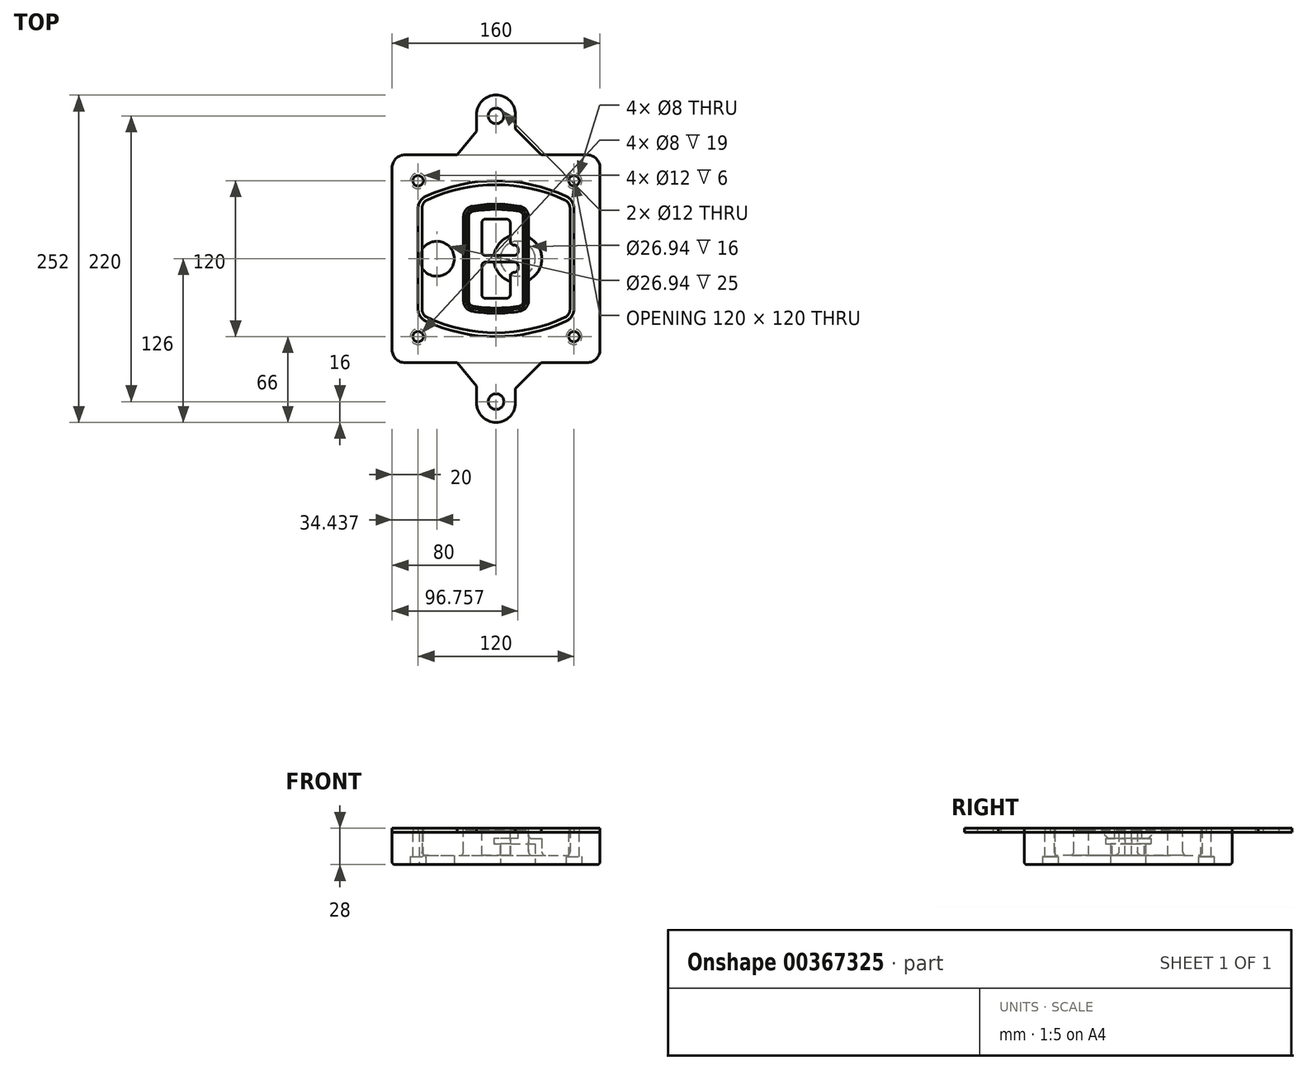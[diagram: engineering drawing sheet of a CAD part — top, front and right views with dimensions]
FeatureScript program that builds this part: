
annotation { "Feature Type Name" : "Feature", "Feature Type Description" : "" }
export const myFeature = defineFeature(function(context is Context, id is Id, definition is map)
    precondition{}
    {
        {
            var Q0;
            Q0=qCreatedBy(makeId("Top.planeOp"),FACE);
            var sketch = newSketch(context, id + "F0", { "sketchPlane" : qUnion([Q0])});
            skPoint(sketch, "E0.rect.middle", {"position": v(0, 0) * mm});
            skLineSegment(sketch, "E1.bottom", {"start": v(-70, -80) * mm, "end": v(70, -80) * mm});
            skLineSegment(sketch, "E1.top", {"start": v(-70, 80) * mm, "end": v(70, 80) * mm});
            skLineSegment(sketch, "E1.left", {"start": v(-80, -70) * mm, "end": v(-80, 70) * mm});
            skLineSegment(sketch, "E1.right", {"start": v(80, -70) * mm, "end": v(80, 70) * mm});
            skLineSegment(sketch, "E2", {"start": v(-80, 80) * mm, "end": v(80, -80) * mm, "construction": true});
            skLineSegment(sketch, "E3", {"start": v(80, 80) * mm, "end": v(-80, -80) * mm, "construction": true});
            skCircle(sketch, "E4", {"center": v(-60, 60) * mm, "radius": 4 * mm});
            skCircle(sketch, "E5", {"center": v(60, 60) * mm, "radius": 4 * mm});
            skCircle(sketch, "E6", {"center": v(60, -60) * mm, "radius": 4 * mm});
            skCircle(sketch, "E7", {"center": v(-60, -60) * mm, "radius": 4 * mm});
            skLineSegment(sketch, "E8", {"start": v(-60, 60) * mm, "end": v(60, 60) * mm, "construction": true});
            skLineSegment(sketch, "E9", {"start": v(60, 60) * mm, "end": v(60, -60) * mm, "construction": true});
            skLineSegment(sketch, "E10", {"start": v(60, -60) * mm, "end": v(-60, -60) * mm, "construction": true});
            skLineSegment(sketch, "E11", {"start": v(-60, -60) * mm, "end": v(-60, 60) * mm, "construction": true});
            skLineSegment(sketch, "E12", {"start": v(-60, 38.83) * mm, "end": v(-60, -38.83) * mm});
            skLineSegment(sketch, "E13", {"start": v(60, 38.83) * mm, "end": v(60, -38.83) * mm});
            skArc(sketch, "E14", {"start": v(54.26, 47.88) * mm, "mid": v(0, 60) * mm, "end": v(-54.26, 47.88) * mm});
            skArc(sketch, "E15", {"start": v(-54.26, -47.88) * mm, "mid": v(0, -60) * mm, "end": v(54.26, -47.88) * mm});
            skLineSegment(sketch, "E16", {"start": v(-60, 0) * mm, "end": v(60, 0) * mm, "construction": true});
            skPoint(sketch, "E17.visualSharp", {"position": v(-60, -45) * mm});
            skArc(sketch, "E17.filletArc", {"start": v(-60, -38.83) * mm, "mid": v(-58.44, -44.2) * mm, "end": v(-54.26, -47.88) * mm});
            skPoint(sketch, "E18.visualSharp", {"position": v(-60, 45) * mm});
            skArc(sketch, "E18.filletArc", {"start": v(-54.26, 47.88) * mm, "mid": v(-58.44, 44.2) * mm, "end": v(-60, 38.83) * mm});
            skPoint(sketch, "E19.visualSharp", {"position": v(60, 45) * mm});
            skArc(sketch, "E19.filletArc", {"start": v(60, 38.83) * mm, "mid": v(58.44, 44.2) * mm, "end": v(54.26, 47.88) * mm});
            skPoint(sketch, "E20.visualSharp", {"position": v(60, -45) * mm});
            skArc(sketch, "E20.filletArc", {"start": v(54.26, -47.88) * mm, "mid": v(58.44, -44.2) * mm, "end": v(60, -38.83) * mm});
            skPoint(sketch, "E21.visualSharp", {"position": v(-80, 80) * mm});
            skArc(sketch, "E21.filletArc", {"start": v(-70, 80) * mm, "mid": v(-77.07, 77.07) * mm, "end": v(-80, 70) * mm});
            skPoint(sketch, "E22.visualSharp", {"position": v(80, 80) * mm});
            skArc(sketch, "E22.filletArc", {"start": v(80, 70) * mm, "mid": v(77.07, 77.07) * mm, "end": v(70, 80) * mm});
            skPoint(sketch, "E23.visualSharp", {"position": v(80, -80) * mm});
            skArc(sketch, "E23.filletArc", {"start": v(70, -80) * mm, "mid": v(77.07, -77.07) * mm, "end": v(80, -70) * mm});
            skPoint(sketch, "E24.visualSharp", {"position": v(-80, -80) * mm});
            skArc(sketch, "E24.filletArc", {"start": v(-80, -70) * mm, "mid": v(-77.07, -77.07) * mm, "end": v(-70, -80) * mm});
            skArc(sketch, "E25.0", {"start": v(57, 38.83) * mm, "mid": v(55.9, 42.58) * mm, "end": v(52.98, 45.17) * mm});
            skLineSegment(sketch, "E25.1", {"start": v(57, 38.83) * mm, "end": v(57, -38.83) * mm});
            skArc(sketch, "E25.2", {"start": v(52.98, -45.17) * mm, "mid": v(55.9, -42.58) * mm, "end": v(57, -38.83) * mm});
            skArc(sketch, "E25.3", {"start": v(-52.98, -45.17) * mm, "mid": v(0, -57) * mm, "end": v(52.98, -45.17) * mm});
            skArc(sketch, "E25.4", {"start": v(-57, -38.83) * mm, "mid": v(-55.9, -42.58) * mm, "end": v(-52.98, -45.17) * mm});
            skArc(sketch, "E25.5", {"start": v(52.98, 45.17) * mm, "mid": v(0, 57) * mm, "end": v(-52.98, 45.17) * mm});
            skLineSegment(sketch, "E25.6", {"start": v(-57, 38.83) * mm, "end": v(-57, -38.83) * mm});
            skArc(sketch, "E25.7", {"start": v(-52.98, 45.17) * mm, "mid": v(-55.9, 42.58) * mm, "end": v(-57, 38.83) * mm});
            skArc(sketch, "E26.0", {"start": v(-55.96, 51.5) * mm, "mid": v(-61.82, 46.33) * mm, "end": v(-64, 38.83) * mm});
            skArc(sketch, "E26.1", {"start": v(55.96, 51.5) * mm, "mid": v(0, 64) * mm, "end": v(-55.96, 51.5) * mm});
            skArc(sketch, "E26.2", {"start": v(64, 38.83) * mm, "mid": v(61.82, 46.33) * mm, "end": v(55.96, 51.5) * mm});
            skLineSegment(sketch, "E26.3", {"start": v(64, 38.83) * mm, "end": v(64, -38.83) * mm});
            skArc(sketch, "E26.4", {"start": v(55.96, -51.5) * mm, "mid": v(61.82, -46.33) * mm, "end": v(64, -38.83) * mm});
            skLineSegment(sketch, "E26.5", {"start": v(-64, 38.83) * mm, "end": v(-64, -38.83) * mm});
            skArc(sketch, "E26.6", {"start": v(-55.96, -51.5) * mm, "mid": v(0, -64) * mm, "end": v(55.96, -51.5) * mm});
            skArc(sketch, "E26.7", {"start": v(-64, -38.83) * mm, "mid": v(-61.82, -46.33) * mm, "end": v(-55.96, -51.5) * mm});
            skSolve(sketch);
        }
        {
            var Q0;
            Q0=makeQuery(id+"F0.imprint","IMPRINT",FACE,{"disambiguationData":[TD([[makeQuery(id+"F0.imprint","IMPRINT",EDGE,{"derivedFrom":sQuery(id+"F0.wireOp",EDGE,"E1.bottom")}),1.0]])]});
            var Q1;
            Q1=makeQuery(id+"F0.imprint","IMPRINT",FACE,{"disambiguationData":[TD([[makeQuery(id+"F0.imprint","IMPRINT",EDGE,{"derivedFrom":sQuery(id+"F0.wireOp",EDGE,"E12")}),1.0]])]});
            var Q2;
            Q2=makeQuery(id+"F0.imprint","IMPRINT",FACE,{"disambiguationData":[TD([[makeQuery(id+"F0.imprint","IMPRINT",EDGE,{"derivedFrom":sQuery(id+"F0.wireOp",EDGE,"E25.0")}),1.0]])]});
            var Q3;
            Q3=makeQuery(id+"F0.imprint","IMPRINT",FACE,{"disambiguationData":[TD([[makeQuery(id+"F0.imprint","IMPRINT",EDGE,{"derivedFrom":sQuery(id+"F0.wireOp",EDGE,"E12")}),-1.0]])]});
            extrude(context, id + "F1", {"entities" : qUnion([Q0, Q1, Q2, Q3]), "oppositeDirection" : true, "depth" : 25 * mm});
        }
        {
            var Q0;
            Q0=makeQuery(id+"F0.imprint","IMPRINT",FACE,{"disambiguationData":[TD([[makeQuery(id+"F0.imprint","IMPRINT",EDGE,{"derivedFrom":sQuery(id+"F0.wireOp",EDGE,"E12")}),1.0]])]});
            extrude(context, id + "F2", {"entities" : qUnion([Q0]), "operationType" : NewBodyOperationType.ADD, "depth" : 3 * mm});
        }
        {
            var Q0;
            Q0=makeQuery(id+"F0.imprint","IMPRINT",FACE,{"disambiguationData":[TD([[makeQuery(id+"F0.imprint","IMPRINT",EDGE,{"derivedFrom":sQuery(id+"F0.wireOp",EDGE,"E25.0")}),1.0]])]});
            extrude(context, id + "F3", {"entities" : qUnion([Q0]), "operationType" : NewBodyOperationType.REMOVE, "oppositeDirection" : true, "depth" : 18 * mm});
        }
        {
            var Q0;
            Q0=makeQuery(id+"F2.opExtrude","CAP_FACE",FACE,{"disambiguationData":[OSD([sQuery(id+"F0.wireOp",EDGE,"E12"),sQuery(id+"F0.wireOp",EDGE,"E13"),sQuery(id+"F0.wireOp",EDGE,"E14"),sQuery(id+"F0.wireOp",EDGE,"E15"),sQuery(id+"F0.wireOp",EDGE,"E17.filletArc"),sQuery(id+"F0.wireOp",EDGE,"E18.filletArc"),sQuery(id+"F0.wireOp",EDGE,"E19.filletArc"),sQuery(id+"F0.wireOp",EDGE,"E20.filletArc"),sQuery(id+"F0.wireOp",EDGE,"E25.0"),sQuery(id+"F0.wireOp",EDGE,"E25.1"),sQuery(id+"F0.wireOp",EDGE,"E25.2"),sQuery(id+"F0.wireOp",EDGE,"E25.3"),sQuery(id+"F0.wireOp",EDGE,"E25.4"),sQuery(id+"F0.wireOp",EDGE,"E25.5"),sQuery(id+"F0.wireOp",EDGE,"E25.6"),sQuery(id+"F0.wireOp",EDGE,"E25.7")])],"isStart":false});
            var sketch = newSketch(context, id + "F4", { "sketchPlane" : qUnion([Q0])});
            skArc(sketch, "E27.0", {"start": v(-18.34, -40.45) * mm, "mid": v(0, -42) * mm, "end": v(18.34, -40.45) * mm});
            skArc(sketch, "E28.0", {"start": v(18.34, 40.45) * mm, "mid": v(0, 42) * mm, "end": v(-18.34, 40.45) * mm});
            skLineSegment(sketch, "E29", {"start": v(-25, 32.57) * mm, "end": v(-25, -32.57) * mm});
            skLineSegment(sketch, "E30", {"start": v(25, 32.57) * mm, "end": v(25, -32.57) * mm});
            skLineSegment(sketch, "E31", {"start": v(-25, 39.1) * mm, "end": v(25, 39.1) * mm, "construction": true});
            skLineSegment(sketch, "E32", {"start": v(-25, -39.1) * mm, "end": v(25, -39.1) * mm, "construction": true});
            skPoint(sketch, "E33.visualSharp", {"position": v(-25, 39.1) * mm});
            skArc(sketch, "E33.filletArc", {"start": v(-18.34, 40.45) * mm, "mid": v(-23.11, 37.73) * mm, "end": v(-25, 32.57) * mm});
            skPoint(sketch, "E34.visualSharp", {"position": v(25, 39.1) * mm});
            skArc(sketch, "E34.filletArc", {"start": v(25, 32.57) * mm, "mid": v(23.11, 37.73) * mm, "end": v(18.34, 40.45) * mm});
            skPoint(sketch, "E35.visualSharp", {"position": v(25, -39.1) * mm});
            skArc(sketch, "E35.filletArc", {"start": v(18.34, -40.45) * mm, "mid": v(23.11, -37.73) * mm, "end": v(25, -32.57) * mm});
            skPoint(sketch, "E36.visualSharp", {"position": v(-25, -39.1) * mm});
            skArc(sketch, "E36.filletArc", {"start": v(-25, -32.57) * mm, "mid": v(-23.11, -37.73) * mm, "end": v(-18.34, -40.45) * mm});
            skArc(sketch, "E37.0", {"start": v(52.98, 45.17) * mm, "mid": v(0, 57) * mm, "end": v(-52.98, 45.17) * mm});
            skArc(sketch, "E37.1", {"start": v(-52.98, 45.17) * mm, "mid": v(-55.9, 42.58) * mm, "end": v(-57, 38.83) * mm});
            skLineSegment(sketch, "E37.2", {"start": v(-57, 38.83) * mm, "end": v(-57, -38.83) * mm});
            skArc(sketch, "E37.3", {"start": v(-57, -38.83) * mm, "mid": v(-55.9, -42.58) * mm, "end": v(-52.98, -45.17) * mm});
            skArc(sketch, "E37.4", {"start": v(-52.98, -45.17) * mm, "mid": v(0, -57) * mm, "end": v(52.98, -45.17) * mm});
            skArc(sketch, "E37.5", {"start": v(52.98, -45.17) * mm, "mid": v(55.9, -42.58) * mm, "end": v(57, -38.83) * mm});
            skLineSegment(sketch, "E37.6", {"start": v(57, 38.83) * mm, "end": v(57, -38.83) * mm});
            skArc(sketch, "E37.7", {"start": v(57, 38.83) * mm, "mid": v(55.9, 42.58) * mm, "end": v(52.98, 45.17) * mm});
            skLineSegment(sketch, "E38.0", {"start": v(23, 32.57) * mm, "end": v(23, -32.57) * mm});
            skArc(sketch, "E38.1", {"start": v(18, -38.48) * mm, "mid": v(21.58, -36.44) * mm, "end": v(23, -32.57) * mm});
            skArc(sketch, "E38.2", {"start": v(-18, -38.48) * mm, "mid": v(0, -40) * mm, "end": v(18, -38.48) * mm});
            skArc(sketch, "E38.3", {"start": v(-23, -32.57) * mm, "mid": v(-21.58, -36.44) * mm, "end": v(-18, -38.48) * mm});
            skLineSegment(sketch, "E38.4", {"start": v(-23, 32.57) * mm, "end": v(-23, -32.57) * mm});
            skArc(sketch, "E38.5", {"start": v(23, 32.57) * mm, "mid": v(21.58, 36.44) * mm, "end": v(18, 38.48) * mm});
            skArc(sketch, "E38.6", {"start": v(-18, 38.48) * mm, "mid": v(-21.58, 36.44) * mm, "end": v(-23, 32.57) * mm});
            skArc(sketch, "E38.7", {"start": v(18, 38.48) * mm, "mid": v(0, 40) * mm, "end": v(-18, 38.48) * mm});
            skArc(sketch, "E39.0", {"start": v(21, 32.57) * mm, "mid": v(20.06, 35.15) * mm, "end": v(17.67, 36.5) * mm});
            skLineSegment(sketch, "E39.1", {"start": v(21, 32.57) * mm, "end": v(21, -32.57) * mm});
            skArc(sketch, "E39.2", {"start": v(17.67, -36.5) * mm, "mid": v(20.06, -35.15) * mm, "end": v(21, -32.57) * mm});
            skArc(sketch, "E39.3", {"start": v(-17.67, -36.5) * mm, "mid": v(0, -38) * mm, "end": v(17.67, -36.5) * mm});
            skArc(sketch, "E39.4", {"start": v(-21, -32.57) * mm, "mid": v(-20.06, -35.15) * mm, "end": v(-17.67, -36.5) * mm});
            skArc(sketch, "E39.5", {"start": v(17.67, 36.5) * mm, "mid": v(0, 38) * mm, "end": v(-17.67, 36.5) * mm});
            skLineSegment(sketch, "E39.6", {"start": v(-21, 32.57) * mm, "end": v(-21, -32.57) * mm});
            skArc(sketch, "E39.7", {"start": v(-17.67, 36.5) * mm, "mid": v(-20.06, 35.15) * mm, "end": v(-21, 32.57) * mm});
            skLineSegment(sketch, "E40", {"start": v(-25, 0) * mm, "end": v(25, 0) * mm, "construction": true});
            skLineSegment(sketch, "E41", {"start": v(-11, 5.5) * mm, "end": v(-11, 27.5) * mm});
            skLineSegment(sketch, "E42", {"start": v(-8, 30.5) * mm, "end": v(8, 30.5) * mm});
            skLineSegment(sketch, "E43", {"start": v(11, 27.5) * mm, "end": v(11, 13.5) * mm});
            skLineSegment(sketch, "E44", {"start": v(14, 10.5) * mm, "end": v(14, 10.5) * mm});
            skLineSegment(sketch, "E45", {"start": v(17, 7.5) * mm, "end": v(17, 5.5) * mm});
            skLineSegment(sketch, "E46", {"start": v(14, 2.5) * mm, "end": v(-8, 2.5) * mm});
            skPoint(sketch, "E47.visualSharp", {"position": v(-11, 30.5) * mm});
            skArc(sketch, "E47.filletArc", {"start": v(-8, 30.5) * mm, "mid": v(-10.12, 29.62) * mm, "end": v(-11, 27.5) * mm});
            skPoint(sketch, "E48.visualSharp", {"position": v(11, 30.5) * mm});
            skArc(sketch, "E48.filletArc", {"start": v(11, 27.5) * mm, "mid": v(10.12, 29.62) * mm, "end": v(8, 30.5) * mm});
            skPoint(sketch, "E49.visualSharp", {"position": v(11, 10.5) * mm});
            skArc(sketch, "E49.filletArc", {"start": v(11, 13.5) * mm, "mid": v(11.88, 11.38) * mm, "end": v(14, 10.5) * mm});
            skPoint(sketch, "E50.visualSharp", {"position": v(17, 10.5) * mm});
            skArc(sketch, "E50.filletArc", {"start": v(17, 7.5) * mm, "mid": v(16.12, 9.62) * mm, "end": v(14, 10.5) * mm});
            skPoint(sketch, "E51.visualSharp", {"position": v(17, 2.5) * mm});
            skArc(sketch, "E51.filletArc", {"start": v(14, 2.5) * mm, "mid": v(16.12, 3.38) * mm, "end": v(17, 5.5) * mm});
            skPoint(sketch, "E52.visualSharp", {"position": v(-11, 2.5) * mm});
            skArc(sketch, "E52.filletArc", {"start": v(-11, 5.5) * mm, "mid": v(-10.12, 3.38) * mm, "end": v(-8, 2.5) * mm});
            skLineSegment(sketch, "E53.0.MirrorCS", {"start": v(14, -2.5) * mm, "end": v(-8, -2.5) * mm});
            skArc(sketch, "E54.0.MirrorCS", {"start": v(-11, -5.5) * mm, "mid": v(-10.12, -3.38) * mm, "end": v(-8, -2.5) * mm});
            skLineSegment(sketch, "E55.0.MirrorCS", {"start": v(-11, -5.5) * mm, "end": v(-11, -27.5) * mm});
            skArc(sketch, "E56.0.MirrorCS", {"start": v(-8, -30.5) * mm, "mid": v(-10.12, -29.62) * mm, "end": v(-11, -27.5) * mm});
            skLineSegment(sketch, "E57.0.MirrorCS", {"start": v(-8, -30.5) * mm, "end": v(8, -30.5) * mm});
            skArc(sketch, "E58.0.MirrorCS", {"start": v(11, -27.5) * mm, "mid": v(10.12, -29.62) * mm, "end": v(8, -30.5) * mm});
            skLineSegment(sketch, "E59.0.MirrorCS", {"start": v(11, -27.5) * mm, "end": v(11, -13.5) * mm});
            skArc(sketch, "E60.0.MirrorCS", {"start": v(11, -13.5) * mm, "mid": v(11.88, -11.38) * mm, "end": v(14, -10.5) * mm});
            skArc(sketch, "E61.0.MirrorCS", {"start": v(17, -7.5) * mm, "mid": v(16.12, -9.62) * mm, "end": v(14, -10.5) * mm});
            skLineSegment(sketch, "E62.0.MirrorCS", {"start": v(17, -7.5) * mm, "end": v(17, -5.5) * mm});
            skArc(sketch, "E63.0.MirrorCS", {"start": v(14, -2.5) * mm, "mid": v(16.12, -3.38) * mm, "end": v(17, -5.5) * mm});
            skSolve(sketch);
        }
        {
            var Q0;
            Q0=makeQuery(id+"F4.imprint","IMPRINT",FACE,{"disambiguationData":[TD([[makeQuery(id+"F4.imprint","IMPRINT",EDGE,{"derivedFrom":sQuery(id+"F4.wireOp",EDGE,"E27.0")}),1.0]])]});
            var Q1;
            Q1=makeQuery(id+"F4.imprint","IMPRINT",FACE,{"disambiguationData":[TD([[makeQuery(id+"F4.imprint","IMPRINT",EDGE,{"derivedFrom":sQuery(id+"F4.wireOp",EDGE,"E38.0")}),-1.0]])]});
            var Q2;
            Q2=makeQuery(id+"F4.imprint","IMPRINT",FACE,{"disambiguationData":[TD([[makeQuery(id+"F4.imprint","IMPRINT",EDGE,{"derivedFrom":sQuery(id+"F4.wireOp",EDGE,"E39.0")}),1.0]])]});
            extrude(context, id + "F5", {"entities" : qUnion([Q0, Q1, Q2]), "operationType" : NewBodyOperationType.ADD, "endBound" : BoundingType.UP_TO_NEXT, "oppositeDirection" : true, "depth" : 25 * mm});
        }
        {
            var Q0;
            Q0=makeQuery(id+"F4.imprint","IMPRINT",FACE,{"disambiguationData":[TD([[makeQuery(id+"F4.imprint","IMPRINT",EDGE,{"derivedFrom":sQuery(id+"F4.wireOp",EDGE,"E38.0")}),-1.0]])]});
            extrude(context, id + "F6", {"entities" : qUnion([Q0]), "operationType" : NewBodyOperationType.REMOVE, "oppositeDirection" : true, "depth" : 2 * mm});
        }
        {
            var Q0;
            Q0=makeQuery(id+"F1.opExtrude","CAP_FACE",FACE,{"disambiguationData":[OSD([sQuery(id+"F0.wireOp",EDGE,"E1.bottom"),sQuery(id+"F0.wireOp",EDGE,"E1.top"),sQuery(id+"F0.wireOp",EDGE,"E1.left"),sQuery(id+"F0.wireOp",EDGE,"E1.right"),sQuery(id+"F0.wireOp",EDGE,"E4"),sQuery(id+"F0.wireOp",EDGE,"E5"),sQuery(id+"F0.wireOp",EDGE,"E6"),sQuery(id+"F0.wireOp",EDGE,"E7"),sQuery(id+"F0.wireOp",EDGE,"E21.filletArc"),sQuery(id+"F0.wireOp",EDGE,"E22.filletArc"),sQuery(id+"F0.wireOp",EDGE,"E23.filletArc"),sQuery(id+"F0.wireOp",EDGE,"E24.filletArc")])],"isStart":false});
            var sketch = newSketch(context, id + "F7", { "sketchPlane" : qUnion([Q0])});
            skCircle(sketch, "E64", {"center": v(16.76, 0) * mm, "radius": 13.47 * mm});
            skCircle(sketch, "E65", {"center": v(-45.56, 0) * mm, "radius": 13.47 * mm});
            skLineSegment(sketch, "E66", {"start": v(80, 0) * mm, "end": v(-80, 0) * mm});
            skCircle(sketch, "E67", {"center": v(16.76, 0) * mm, "radius": 18.47 * mm});
            skCircle(sketch, "E68", {"center": v(60, -60) * mm, "radius": 6 * mm});
            skCircle(sketch, "E69", {"center": v(-60, -60) * mm, "radius": 6 * mm});
            skCircle(sketch, "E70", {"center": v(-60, 60) * mm, "radius": 6 * mm});
            skCircle(sketch, "E71", {"center": v(60, 60) * mm, "radius": 6 * mm});
            skSolve(sketch);
        }
        {
            var Q0;
            {var subQ1=sQuery(id+"F7.wireOp",EDGE,"E66");var subQ4=sQuery(id+"F7.wireOp",EDGE,"E64");var subQ6=makeQuery(id+"F7.imprint","INTERSECT",VERTEX,{"disambiguationData":[OD(0.0)],"derivedFrom":[subQ4,subQ1]});Q0=makeQuery(id+"F7.imprint","IMPRINT",FACE,{"disambiguationData":[TD([[makeQuery(id+"F7.imprint","IMPRINT",EDGE,{"disambiguationData":[TD([[subQ6,-1.0]])],"derivedFrom":subQ4}),-1.0]])]});}
            var Q1;
            {var subQ0=sQuery(id+"F7.wireOp",EDGE,"E66");var subQ1=sQuery(id+"F7.wireOp",EDGE,"E64");var subQ3=makeQuery(id+"F7.imprint","INTERSECT",VERTEX,{"disambiguationData":[OD(0.0)],"derivedFrom":[subQ1,subQ0]});Q1=makeQuery(id+"F7.imprint","IMPRINT",FACE,{"disambiguationData":[TD([[makeQuery(id+"F7.imprint","IMPRINT",EDGE,{"disambiguationData":[TD([[subQ3,-1.0]])],"derivedFrom":subQ1}),1.0]])]});}
            var Q2;
            {var subQ0=sQuery(id+"F7.wireOp",EDGE,"E66");var subQ1=sQuery(id+"F7.wireOp",EDGE,"E64");var subQ3=makeQuery(id+"F7.imprint","INTERSECT",VERTEX,{"disambiguationData":[OD(0.0)],"derivedFrom":[subQ1,subQ0]});Q2=makeQuery(id+"F7.imprint","IMPRINT",FACE,{"disambiguationData":[TD([[makeQuery(id+"F7.imprint","IMPRINT",EDGE,{"disambiguationData":[TD([[subQ3,1.0]])],"derivedFrom":subQ1}),1.0]])]});}
            var Q3;
            {var subQ1=sQuery(id+"F7.wireOp",EDGE,"E66");var subQ4=sQuery(id+"F7.wireOp",EDGE,"E64");var subQ6=makeQuery(id+"F7.imprint","INTERSECT",VERTEX,{"disambiguationData":[OD(0.0)],"derivedFrom":[subQ4,subQ1]});Q3=makeQuery(id+"F7.imprint","IMPRINT",FACE,{"disambiguationData":[TD([[makeQuery(id+"F7.imprint","IMPRINT",EDGE,{"disambiguationData":[TD([[subQ6,1.0]])],"derivedFrom":subQ4}),-1.0]])]});}
            extrude(context, id + "F8", {"entities" : qUnion([Q0, Q1, Q2, Q3]), "operationType" : NewBodyOperationType.ADD, "oppositeDirection" : true, "depth" : 20 * mm});
        }
        {
            var Q0;
            {var subQ0=sQuery(id+"F7.wireOp",EDGE,"E66");var subQ1=sQuery(id+"F7.wireOp",EDGE,"E64");var subQ3=makeQuery(id+"F7.imprint","INTERSECT",VERTEX,{"disambiguationData":[OD(0.0)],"derivedFrom":[subQ1,subQ0]});Q0=makeQuery(id+"F7.imprint","IMPRINT",FACE,{"disambiguationData":[TD([[makeQuery(id+"F7.imprint","IMPRINT",EDGE,{"disambiguationData":[TD([[subQ3,-1.0]])],"derivedFrom":subQ1}),1.0]])]});}
            var Q1;
            {var subQ0=sQuery(id+"F7.wireOp",EDGE,"E66");var subQ1=sQuery(id+"F7.wireOp",EDGE,"E64");var subQ3=makeQuery(id+"F7.imprint","INTERSECT",VERTEX,{"disambiguationData":[OD(0.0)],"derivedFrom":[subQ1,subQ0]});Q1=makeQuery(id+"F7.imprint","IMPRINT",FACE,{"disambiguationData":[TD([[makeQuery(id+"F7.imprint","IMPRINT",EDGE,{"disambiguationData":[TD([[subQ3,1.0]])],"derivedFrom":subQ1}),1.0]])]});}
            extrude(context, id + "F9", {"entities" : qUnion([Q0, Q1]), "operationType" : NewBodyOperationType.REMOVE, "oppositeDirection" : true, "depth" : 16 * mm});
        }
        {
            var Q0;
            {var subQ0=sQuery(id+"F7.wireOp",EDGE,"E66");var subQ1=sQuery(id+"F7.wireOp",EDGE,"E65");var subQ3=makeQuery(id+"F7.imprint","INTERSECT",VERTEX,{"disambiguationData":[OD(0.0)],"derivedFrom":[subQ1,subQ0]});Q0=makeQuery(id+"F7.imprint","IMPRINT",FACE,{"disambiguationData":[TD([[makeQuery(id+"F7.imprint","IMPRINT",EDGE,{"disambiguationData":[TD([[subQ3,-1.0]])],"derivedFrom":subQ1}),1.0]])]});}
            var Q1;
            {var subQ0=sQuery(id+"F7.wireOp",EDGE,"E66");var subQ1=sQuery(id+"F7.wireOp",EDGE,"E65");var subQ3=makeQuery(id+"F7.imprint","INTERSECT",VERTEX,{"disambiguationData":[OD(0.0)],"derivedFrom":[subQ1,subQ0]});Q1=makeQuery(id+"F7.imprint","IMPRINT",FACE,{"disambiguationData":[TD([[makeQuery(id+"F7.imprint","IMPRINT",EDGE,{"disambiguationData":[TD([[subQ3,1.0]])],"derivedFrom":subQ1}),1.0]])]});}
            extrude(context, id + "F10", {"entities" : qUnion([Q0, Q1]), "operationType" : NewBodyOperationType.REMOVE, "oppositeDirection" : true, "depth" : 25 * mm});
        }
        {
            var Q0;
            Q0=makeQuery(id+"F7.imprint","IMPRINT",FACE,{"disambiguationData":[TD([[makeQuery(id+"F7.imprint","IMPRINT",EDGE,{"derivedFrom":sQuery(id+"F7.wireOp",EDGE,"E68")}),1.0]])]});
            var Q1;
            Q1=makeQuery(id+"F7.imprint","IMPRINT",FACE,{"disambiguationData":[TD([[makeQuery(id+"F7.imprint","IMPRINT",EDGE,{"derivedFrom":makeQuery(id+"F1.opExtrude","CAP_EDGE",EDGE,{"disambiguationData":[OSD([sQuery(id+"F0.wireOp",EDGE,"E5")])],"isStart":false})}),-1.0]])]});
            var Q2;
            Q2=makeQuery(id+"F7.imprint","IMPRINT",FACE,{"disambiguationData":[TD([[makeQuery(id+"F7.imprint","IMPRINT",EDGE,{"derivedFrom":sQuery(id+"F7.wireOp",EDGE,"E69")}),1.0]])]});
            var Q3;
            Q3=makeQuery(id+"F7.imprint","IMPRINT",FACE,{"disambiguationData":[TD([[makeQuery(id+"F7.imprint","IMPRINT",EDGE,{"derivedFrom":makeQuery(id+"F1.opExtrude","CAP_EDGE",EDGE,{"disambiguationData":[OSD([sQuery(id+"F0.wireOp",EDGE,"E4")])],"isStart":false})}),-1.0]])]});
            var Q4;
            Q4=makeQuery(id+"F7.imprint","IMPRINT",FACE,{"disambiguationData":[TD([[makeQuery(id+"F7.imprint","IMPRINT",EDGE,{"derivedFrom":sQuery(id+"F7.wireOp",EDGE,"E70")}),1.0]])]});
            var Q5;
            Q5=makeQuery(id+"F7.imprint","IMPRINT",FACE,{"disambiguationData":[TD([[makeQuery(id+"F7.imprint","IMPRINT",EDGE,{"derivedFrom":makeQuery(id+"F1.opExtrude","CAP_EDGE",EDGE,{"disambiguationData":[OSD([sQuery(id+"F0.wireOp",EDGE,"E7")])],"isStart":false})}),-1.0]])]});
            var Q6;
            Q6=makeQuery(id+"F7.imprint","IMPRINT",FACE,{"disambiguationData":[TD([[makeQuery(id+"F7.imprint","IMPRINT",EDGE,{"derivedFrom":sQuery(id+"F7.wireOp",EDGE,"E71")}),1.0]])]});
            var Q7;
            Q7=makeQuery(id+"F7.imprint","IMPRINT",FACE,{"disambiguationData":[TD([[makeQuery(id+"F7.imprint","IMPRINT",EDGE,{"derivedFrom":makeQuery(id+"F1.opExtrude","CAP_EDGE",EDGE,{"disambiguationData":[OSD([sQuery(id+"F0.wireOp",EDGE,"E6")])],"isStart":false})}),-1.0]])]});
            extrude(context, id + "F11", {"entities" : qUnion([Q0, Q1, Q2, Q3, Q4, Q5, Q6, Q7]), "operationType" : NewBodyOperationType.REMOVE, "oppositeDirection" : true, "depth" : 6 * mm});
        }
        {
            var Q0;
            Q0=makeQuery(id+"F9.boolean.opBoolean","COPY",FACE,{"derivedFrom":makeQuery(id+"F9.opExtrude","CAP_FACE",FACE,{"disambiguationData":[OSD([sQuery(id+"F7.wireOp",EDGE,"E64")])],"isStart":false})});
            var sketch = newSketch(context, id + "F12", { "sketchPlane" : qUnion([Q0])});
            skArc(sketch, "E72.0", {"start": v(11, 17.55) * mm, "mid": v(2.57, 11.82) * mm, "end": v(-1.54, 2.5) * mm});
            skArc(sketch, "E72.1", {"start": v(-1.54, -2.5) * mm, "mid": v(2.57, -11.82) * mm, "end": v(11, -17.55) * mm});
            skLineSegment(sketch, "E73", {"start": v(-1.54, -2.5) * mm, "end": v(14, -2.5) * mm});
            skLineSegment(sketch, "E74.0", {"start": v(14, 2.5) * mm, "end": v(-1.54, 2.5) * mm});
            skArc(sketch, "E74.1", {"start": v(14, 2.5) * mm, "mid": v(16.12, 3.38) * mm, "end": v(17, 5.5) * mm});
            skLineSegment(sketch, "E74.2", {"start": v(17, 7.5) * mm, "end": v(17, 5.5) * mm});
            skArc(sketch, "E74.3", {"start": v(17, 7.5) * mm, "mid": v(16.12, 9.62) * mm, "end": v(14, 10.5) * mm});
            skArc(sketch, "E74.4", {"start": v(11, 13.5) * mm, "mid": v(11.88, 11.38) * mm, "end": v(14, 10.5) * mm});
            skLineSegment(sketch, "E74.5", {"start": v(11, 17.55) * mm, "end": v(11, 13.5) * mm});
            skLineSegment(sketch, "E74.7", {"start": v(14, -2.5) * mm, "end": v(-1.54, -2.5) * mm});
            skArc(sketch, "E74.8", {"start": v(14, -2.5) * mm, "mid": v(16.12, -3.38) * mm, "end": v(17, -5.5) * mm});
            skLineSegment(sketch, "E74.9", {"start": v(17, -7.5) * mm, "end": v(17, -5.5) * mm});
            skArc(sketch, "E74.10", {"start": v(17, -7.5) * mm, "mid": v(16.12, -9.62) * mm, "end": v(14, -10.5) * mm});
            skArc(sketch, "E74.11", {"start": v(11, -13.5) * mm, "mid": v(11.88, -11.38) * mm, "end": v(14, -10.5) * mm});
            skLineSegment(sketch, "E74.12", {"start": v(11, -17.55) * mm, "end": v(11, -13.5) * mm});
            skPoint(sketch, "E75.orphan", {"position": v(11, -27.5) * mm});
            skPoint(sketch, "E76.orphan", {"position": v(-8, -2.5) * mm});
            skPoint(sketch, "E77.orphan", {"position": v(-8, 2.5) * mm});
            skPoint(sketch, "E78.orphan", {"position": v(11, 27.5) * mm});
            skSolve(sketch);
        }
        {
            var Q0;
            {var subQ7=sQuery(id+"F12.wireOp",EDGE,"E72.0");var subQ14=sQuery(id+"F12.wireOp",EDGE,"E72.1");var subQ16=sQuery(id+"F12.wireOp",EDGE,"E74.1");var subQ18=sQuery(id+"F12.wireOp",EDGE,"E74.8");Q0=qUnion([makeQuery(id+"F12.imprint","IMPRINT",FACE,{"disambiguationData":[TD([[makeQuery(id+"F12.imprint","IMPRINT",EDGE,{"derivedFrom":subQ7}),1.0]])]}),makeQuery(id+"F12.imprint","IMPRINT",FACE,{"disambiguationData":[TD([[makeQuery(id+"F12.imprint","IMPRINT",EDGE,{"derivedFrom":subQ14}),1.0]])]}),makeQuery(id+"F12.imprint","IMPRINT",FACE,{"disambiguationData":[TD([[makeQuery(id+"F12.imprint","IMPRINT",EDGE,{"derivedFrom":subQ16}),1.0]])]}),makeQuery(id+"F12.imprint","IMPRINT",FACE,{"disambiguationData":[TD([[makeQuery(id+"F12.imprint","IMPRINT",EDGE,{"derivedFrom":subQ18}),-1.0]])]})]);}
            var Q1;
            Q1=makeQuery(id+"F5.boolean.opBoolean","SPLIT",FACE,{"disambiguationData":[TD([makeQuery(id+"F5.opExtrude","SWEPT_FACE",FACE,{"disambiguationData":[OSD([sQuery(id+"F4.wireOp",EDGE,"E41")])]})])],"derivedFrom":makeQuery(id+"F3.boolean.opBoolean","COPY",FACE,{"derivedFrom":makeQuery(id+"F3.opExtrude","CAP_FACE",FACE,{"disambiguationData":[OSD([sQuery(id+"F0.wireOp",EDGE,"E25.0"),sQuery(id+"F0.wireOp",EDGE,"E25.1"),sQuery(id+"F0.wireOp",EDGE,"E25.2"),sQuery(id+"F0.wireOp",EDGE,"E25.3"),sQuery(id+"F0.wireOp",EDGE,"E25.4"),sQuery(id+"F0.wireOp",EDGE,"E25.5"),sQuery(id+"F0.wireOp",EDGE,"E25.6"),sQuery(id+"F0.wireOp",EDGE,"E25.7")])],"isStart":false})})});
            extrude(context, id + "F13", {"entities" : qUnion([Q0]), "operationType" : NewBodyOperationType.REMOVE, "endBound" : BoundingType.UP_TO_SURFACE, "endBoundEntityFace" : qUnion([Q1]), "depth" : 25 * mm});
        }
        {
            var Q0;
            Q0=makeQuery(id+"F3.boolean.opBoolean","COPY",EDGE,{"derivedFrom":makeQuery(id+"F3.opExtrude","CAP_EDGE",EDGE,{"disambiguationData":[OSD([sQuery(id+"F0.wireOp",EDGE,"E25.6")])],"isStart":false})});
            var Q1;
            Q1=makeQuery(id+"F8.boolean.opBoolean","INTERSECT",EDGE,{"derivedFrom":[makeQuery(id+"F5.opExtrude","SWEPT_FACE",FACE,{"disambiguationData":[OSD([sQuery(id+"F4.wireOp",EDGE,"E30")])]}),makeQuery(id+"F8.opExtrude","CAP_FACE",FACE,{"disambiguationData":[OSD([sQuery(id+"F7.wireOp",EDGE,"E67")])],"isStart":false})]});
            var Q2;
            Q2=makeQuery(id+"F8.boolean.opBoolean","INTERSECT",EDGE,{"disambiguationData":[OD(1.0)],"derivedFrom":[makeQuery(id+"F5.opExtrude","SWEPT_FACE",FACE,{"disambiguationData":[OSD([sQuery(id+"F4.wireOp",EDGE,"E30")])]}),makeQuery(id+"F8.opExtrude","SWEPT_FACE",FACE,{"disambiguationData":[OSD([sQuery(id+"F7.wireOp",EDGE,"E67")])]})]});
            var Q3;
            {var subQ0=sQuery(id+"F4.wireOp",EDGE,"E30");Q3=makeQuery(id+"F8.boolean.opBoolean","SPLIT",EDGE,{"disambiguationData":[TD([makeQuery(id+"F5.opExtrude","SWEPT_FACE",FACE,{"disambiguationData":[OSD([sQuery(id+"F4.wireOp",EDGE,"E35.filletArc")])]})])],"derivedFrom":makeQuery(id+"F5.opExtrude","CAP_EDGE",EDGE,{"disambiguationData":[OSD([subQ0])],"isStart":false})});}
            var Q4;
            {var subQ0=sQuery(id+"F0.wireOp",EDGE,"E25.7");var subQ1=sQuery(id+"F0.wireOp",EDGE,"E25.1");var subQ2=sQuery(id+"F0.wireOp",EDGE,"E25.6");var subQ3=sQuery(id+"F0.wireOp",EDGE,"E25.5");var subQ4=sQuery(id+"F0.wireOp",EDGE,"E25.4");var subQ5=sQuery(id+"F0.wireOp",EDGE,"E25.0");var subQ6=sQuery(id+"F0.wireOp",EDGE,"E25.2");var subQ7=sQuery(id+"F0.wireOp",EDGE,"E25.3");Q4=makeQuery(id+"F8.boolean.opBoolean","INTERSECT",EDGE,{"derivedFrom":[makeQuery(id+"F5.boolean.opBoolean","SPLIT",FACE,{"disambiguationData":[TD([makeQuery(id+"F2.opExtrude","SWEPT_FACE",FACE,{"disambiguationData":[OSD([subQ5])]})])],"derivedFrom":makeQuery(id+"F3.boolean.opBoolean","COPY",FACE,{"derivedFrom":makeQuery(id+"F3.opExtrude","CAP_FACE",FACE,{"disambiguationData":[OSD([subQ5,subQ1,subQ6,subQ7,subQ4,subQ3,subQ2,subQ0])],"isStart":false})})}),makeQuery(id+"F8.opExtrude","SWEPT_FACE",FACE,{"disambiguationData":[OSD([sQuery(id+"F7.wireOp",EDGE,"E67")])]})]});}
            var Q5;
            Q5=makeQuery(id+"F8.boolean.opBoolean","INTERSECT",EDGE,{"disambiguationData":[OD(0.0)],"derivedFrom":[makeQuery(id+"F5.opExtrude","SWEPT_FACE",FACE,{"disambiguationData":[OSD([sQuery(id+"F4.wireOp",EDGE,"E30")])]}),makeQuery(id+"F8.opExtrude","SWEPT_FACE",FACE,{"disambiguationData":[OSD([sQuery(id+"F7.wireOp",EDGE,"E67")])]})]});
            fillet(context, id + "F14", {"entities" : qUnion([Q0, Q1, Q2, Q3, Q4, Q5]), "radius" : 3 * mm, "tangentPropagation" : true, "allowEdgeOverflow" : false});
        }
        {
            var Q0;
            Q0=makeQuery(id+"F1.opExtrude","CAP_EDGE",EDGE,{"disambiguationData":[OSD([sQuery(id+"F0.wireOp",EDGE,"E1.bottom")])],"isStart":false});
            fillet(context, id + "F15", {"entities" : qUnion([Q0]), "radius" : 2 * mm, "tangentPropagation" : true, "allowEdgeOverflow" : false});
        }
        {
            var Q0;
            {var subQ0=sQuery(id+"F0.wireOp",EDGE,"E21.filletArc");var subQ1=sQuery(id+"F0.wireOp",EDGE,"E7");var subQ2=sQuery(id+"F0.wireOp",EDGE,"E6");var subQ3=sQuery(id+"F0.wireOp",EDGE,"E5");var subQ4=sQuery(id+"F0.wireOp",EDGE,"E4");var subQ5=sQuery(id+"F0.wireOp",EDGE,"E22.filletArc");var subQ6=sQuery(id+"F0.wireOp",EDGE,"E1.bottom");var subQ7=sQuery(id+"F0.wireOp",EDGE,"E1.right");var subQ8=sQuery(id+"F0.wireOp",EDGE,"E1.top");var subQ9=sQuery(id+"F0.wireOp",EDGE,"E1.left");var subQ10=sQuery(id+"F0.wireOp",EDGE,"E23.filletArc");var subQ11=sQuery(id+"F0.wireOp",EDGE,"E24.filletArc");Q0=makeQuery(id+"F2.boolean.opBoolean","SPLIT",FACE,{"disambiguationData":[TD([makeQuery(id+"F1.opExtrude","SWEPT_FACE",FACE,{"disambiguationData":[OSD([subQ6])]})])],"derivedFrom":makeQuery(id+"F1.opExtrude","CAP_FACE",FACE,{"disambiguationData":[OSD([subQ6,subQ8,subQ9,subQ7,subQ4,subQ3,subQ2,subQ1,subQ0,subQ5,subQ10,subQ11])],"isStart":true})});}
            var sketch = newSketch(context, id + "F16", { "sketchPlane" : qUnion([Q0])});
            skLineSegment(sketch, "E79", {"start": v(0, 80) * mm, "end": v(0, 110) * mm, "construction": true});
            skCircle(sketch, "E80", {"center": v(0, 110) * mm, "radius": 6 * mm});
            skLineSegment(sketch, "E81", {"start": v(-15, 98) * mm, "end": v(-29.8, 80) * mm});
            skLineSegment(sketch, "E82", {"start": v(15, 99.98) * mm, "end": v(34.98, 80) * mm});
            skLineSegment(sketch, "E83", {"start": v(-15, 98) * mm, "end": v(-15, 111) * mm});
            skLineSegment(sketch, "E84", {"start": v(15, 99.98) * mm, "end": v(15, 111) * mm});
            skArc(sketch, "E85", {"start": v(15, 111) * mm, "mid": v(0, 126) * mm, "end": v(-15, 111) * mm});
            skLineSegment(sketch, "E86", {"start": v(-80, 0) * mm, "end": v(80, 0) * mm, "construction": true});
            skLineSegment(sketch, "E87.MirrorCS", {"start": v(15, -99.98) * mm, "end": v(34.98, -80) * mm});
            skArc(sketch, "E88.MirrorCS", {"start": v(15, -111) * mm, "mid": v(0, -126) * mm, "end": v(-15, -111) * mm});
            skLineSegment(sketch, "E89.MirrorCS", {"start": v(0, -80) * mm, "end": v(0, -110) * mm, "construction": true});
            skLineSegment(sketch, "E90.MirrorCS", {"start": v(15, -99.98) * mm, "end": v(15, -111) * mm});
            skLineSegment(sketch, "E91.MirrorCS", {"start": v(-15, -98) * mm, "end": v(-15, -111) * mm});
            skLineSegment(sketch, "E92.MirrorCS", {"start": v(-15, -98) * mm, "end": v(-29.8, -80) * mm});
            skCircle(sketch, "E93.MirrorC", {"center": v(0, -110) * mm, "radius": 6 * mm});
            skSolve(sketch);
        }
        {
            var Q0;
            Q0=makeQuery(id+"F16.imprint","IMPRINT",FACE,{"disambiguationData":[TD([[makeQuery(id+"F16.imprint","IMPRINT",EDGE,{"derivedFrom":sQuery(id+"F16.wireOp",EDGE,"E80")}),-1.0]])]});
            var Q1;
            {var subQ0=sQuery(id+"F16.wireOp",EDGE,"E87.MirrorCS");Q1=makeQuery(id+"F16.imprint","IMPRINT",FACE,{"disambiguationData":[TD([[makeQuery(id+"F16.imprint","IMPRINT",EDGE,{"derivedFrom":subQ0}),1.0]])]});}
            var Q2;
            Q2=makeQuery(id+"F16.imprint","IMPRINT",FACE,{"disambiguationData":[TD([[makeQuery(id+"F16.imprint","IMPRINT",EDGE,{"derivedFrom":makeQuery(id+"F1.opExtrude","CAP_EDGE",EDGE,{"disambiguationData":[OSD([sQuery(id+"F0.wireOp",EDGE,"E1.left")])],"isStart":true})}),-1.0]])]});
            var Q3;
            Q3=makeQuery(id+"F2.opExtrude","CAP_FACE",FACE,{"disambiguationData":[OSD([sQuery(id+"F0.wireOp",EDGE,"E12"),sQuery(id+"F0.wireOp",EDGE,"E13"),sQuery(id+"F0.wireOp",EDGE,"E14"),sQuery(id+"F0.wireOp",EDGE,"E15"),sQuery(id+"F0.wireOp",EDGE,"E17.filletArc"),sQuery(id+"F0.wireOp",EDGE,"E18.filletArc"),sQuery(id+"F0.wireOp",EDGE,"E19.filletArc"),sQuery(id+"F0.wireOp",EDGE,"E20.filletArc"),sQuery(id+"F0.wireOp",EDGE,"E25.0"),sQuery(id+"F0.wireOp",EDGE,"E25.1"),sQuery(id+"F0.wireOp",EDGE,"E25.2"),sQuery(id+"F0.wireOp",EDGE,"E25.3"),sQuery(id+"F0.wireOp",EDGE,"E25.4"),sQuery(id+"F0.wireOp",EDGE,"E25.5"),sQuery(id+"F0.wireOp",EDGE,"E25.6"),sQuery(id+"F0.wireOp",EDGE,"E25.7")])],"isStart":false});
            extrude(context, id + "F17", {"entities" : qUnion([Q0, Q1, Q2]), "endBound" : BoundingType.UP_TO_SURFACE, "endBoundEntityFace" : qUnion([Q3]), "depth" : 25 * mm});
        }
    });
